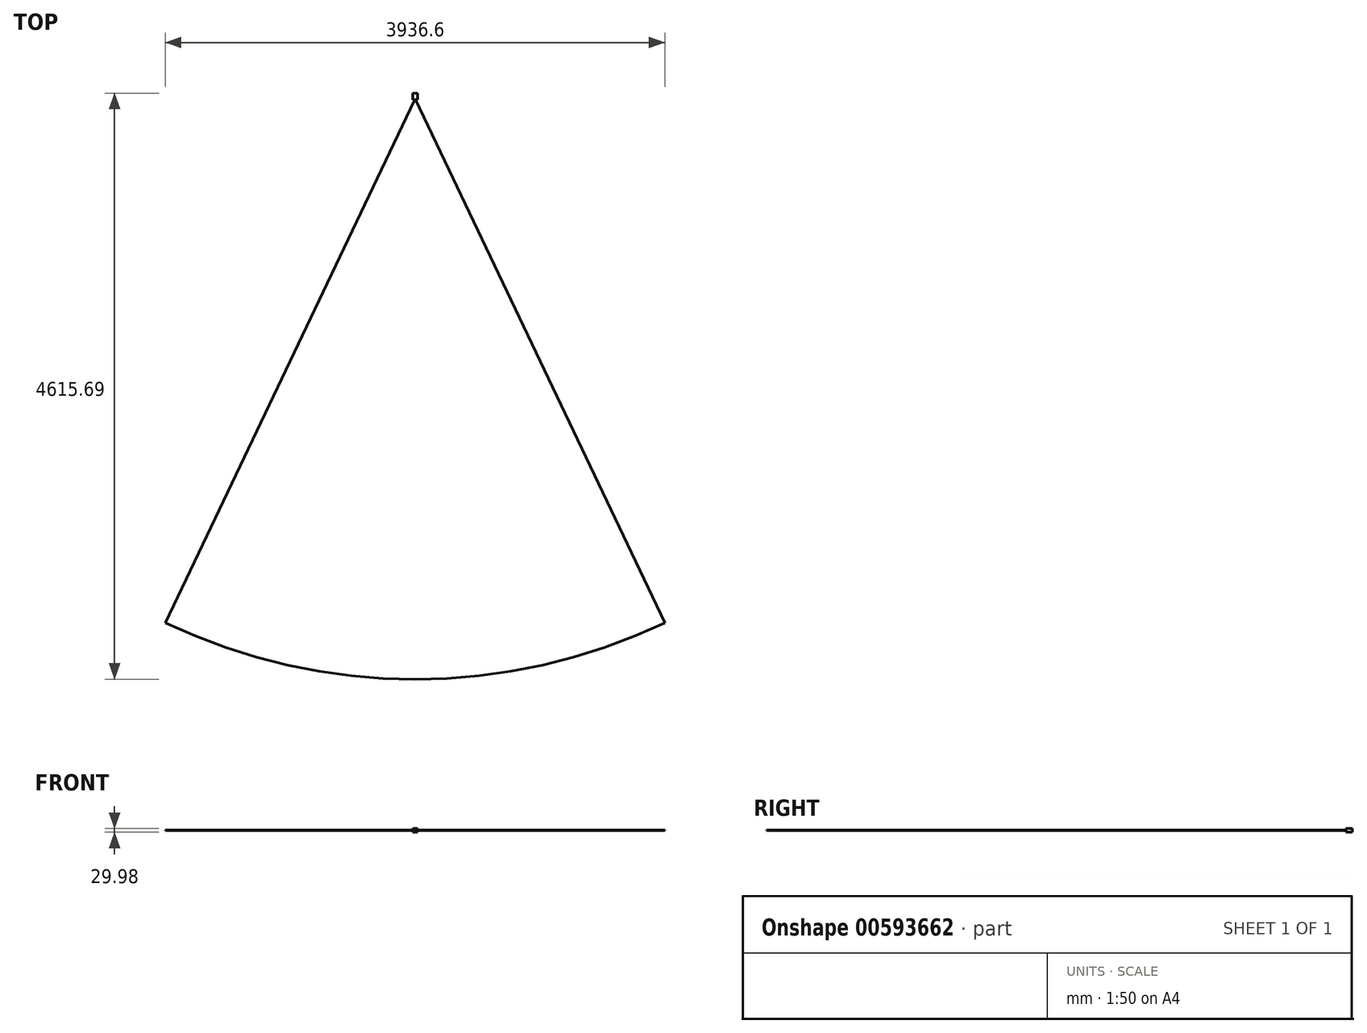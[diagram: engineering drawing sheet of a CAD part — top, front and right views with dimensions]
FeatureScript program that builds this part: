
annotation { "Feature Type Name" : "Feature", "Feature Type Description" : "" }
export const myFeature = defineFeature(function(context is Context, id is Id, definition is map)
    precondition{}
    {
        {
            var Q0;
            Q0=qCreatedBy(makeId("Front.planeOp"),FACE);
            var sketch = newSketch(context, id + "F0", { "sketchPlane" : qUnion([Q0])});
            skLineSegment(sketch, "E0.bottom", {"start": v(19.94, -14.99) * mm, "end": v(-19.94, -14.99) * mm});
            skLineSegment(sketch, "E0.top", {"start": v(19.94, 14.99) * mm, "end": v(-19.94, 14.99) * mm});
            skLineSegment(sketch, "E0.left", {"start": v(19.94, -14.99) * mm, "end": v(19.94, 14.99) * mm});
            skLineSegment(sketch, "E0.right", {"start": v(-19.94, -14.99) * mm, "end": v(-19.94, 14.99) * mm});
            skPoint(sketch, "E0.middle", {"position": v(0, 0) * mm});
            skSolve(sketch);
        }
        {
            var Q0;
            Q0 = qSketchRegion(id + "F0", true);
            extrude(context, id + "F1", {"entities" : qUnion([Q0]), "depth" : 50.04 * mm, "offsetDistance" : 25.4 * mm});
        }
        {
            var Q0;
            Q0=qCreatedBy(makeId("Top.planeOp"),FACE);
            var sketch = newSketch(context, id + "F2", { "sketchPlane" : qUnion([Q0])});
            skLineSegment(sketch, "E1.0", {"start": v(19.94, -50.04) * mm, "end": v(-19.94, -50.04) * mm, "construction": true});
            skLineSegment(sketch, "E2", {"start": v(0, -50.04) * mm, "end": v(0, -43.69) * mm, "construction": true});
            skPoint(sketch, "E2.endSnap0", {"position": v(0, -50.04) * mm});
            skLineSegment(sketch, "E3", {"start": v(0, -43.69) * mm, "end": v(-1968.3, -4170.3) * mm});
            skLineSegment(sketch, "E4.MirrorCS", {"start": v(0, -43.69) * mm, "end": v(1968.3, -4170.3) * mm});
            skArc(sketch, "E5", {"start": v(-1968.3, -4170.3) * mm, "mid": v(0, -4615.69) * mm, "end": v(1968.3, -4170.3) * mm});
            skSolve(sketch);
        }
        {
            var Q0;
            Q0 = qSketchRegion(id + "F2", true);
            extrude(context, id + "F3", {"entities" : qUnion([Q0]), "endBound" : BoundingType.SYMMETRIC, "depth" : 1.9 * mm, "offsetDistance" : 25.4 * mm});
        }
    });
